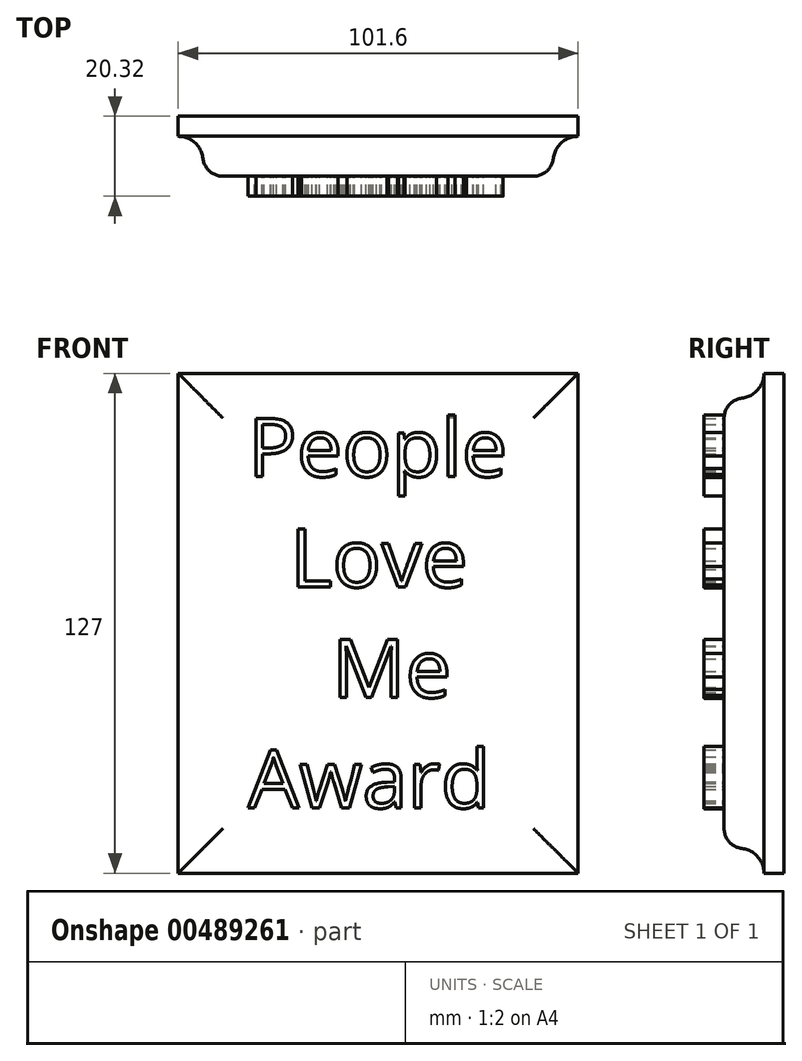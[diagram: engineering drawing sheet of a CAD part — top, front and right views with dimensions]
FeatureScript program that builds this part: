
annotation { "Feature Type Name" : "Feature", "Feature Type Description" : "" }
export const myFeature = defineFeature(function(context is Context, id is Id, definition is map)
    precondition{}
    {
        {
            var Q0;
            Q0=qCreatedBy(makeId("Front.planeOp"),FACE);
            var sketch = newSketch(context, id + "F0", { "sketchPlane" : qUnion([Q0])});
            skLineSegment(sketch, "E0.bottom", {"start": v(-101.6, 127) * mm, "end": v(0, 127) * mm});
            skLineSegment(sketch, "E0.top", {"start": v(-101.6, 0) * mm, "end": v(0, 0) * mm});
            skLineSegment(sketch, "E0.left", {"start": v(-101.6, 127) * mm, "end": v(-101.6, 0) * mm});
            skLineSegment(sketch, "E0.right", {"start": v(0, 127) * mm, "end": v(0, 0) * mm});
            skSolve(sketch);
        }
        {
            var Q0;
            Q0=qSketchRegion(id+"F0",true);
            extrude(context, id + "F1", {"entities" : qUnion([Q0]), "depth" : 15.24 * mm});
        }
        {
            var Q0;
            Q0=makeQuery(id+"F1.opExtrude","CAP_FACE",FACE,{"disambiguationData":[OSD([sQuery(id+"F0.wireOp",EDGE,"E0.bottom"),sQuery(id+"F0.wireOp",EDGE,"E0.top"),sQuery(id+"F0.wireOp",EDGE,"E0.left"),sQuery(id+"F0.wireOp",EDGE,"E0.right")])],"isStart":false});
            var sketch = newSketch(context, id + "F2", { "sketchPlane" : qUnion([Q0])});
            skLineSegment(sketch, "E1.bottom", {"start": v(-6.35, 6.35) * mm, "end": v(-95.25, 6.35) * mm});
            skLineSegment(sketch, "E1.top", {"start": v(-6.35, 120.65) * mm, "end": v(-95.25, 120.65) * mm});
            skLineSegment(sketch, "E1.left", {"start": v(-6.35, 6.35) * mm, "end": v(-6.35, 120.65) * mm});
            skLineSegment(sketch, "E1.right", {"start": v(-95.25, 6.35) * mm, "end": v(-95.25, 120.65) * mm});
            skLineSegment(sketch, "E2.bottom", {"start": v(-101.6, 127) * mm, "end": v(0, 127) * mm});
            skLineSegment(sketch, "E2.top", {"start": v(-101.6, 0) * mm, "end": v(0, 0) * mm});
            skLineSegment(sketch, "E2.left", {"start": v(-101.6, 127) * mm, "end": v(-101.6, 0) * mm});
            skLineSegment(sketch, "E2.right", {"start": v(0, 127) * mm, "end": v(0, 0) * mm});
            skSolve(sketch);
        }
        {
            var Q0;
            Q0=qSketchRegion(id+"F2",true);
            extrude(context, id + "F3", {"entities" : qUnion([Q0]), "operationType" : NewBodyOperationType.REMOVE, "oppositeDirection" : true, "depth" : 10.16 * mm});
        }
        {
            var Q0;
            Q0=makeQuery(id+"F3.boolean.opBoolean","COPY",EDGE,{"derivedFrom":makeQuery(id+"F3.opExtrude","CAP_EDGE",EDGE,{"disambiguationData":[OSD([sQuery(id+"F2.wireOp",EDGE,"E1.top")])],"isStart":false})});
            var Q1;
            Q1=makeQuery(id+"F3.boolean.opBoolean","COPY",EDGE,{"derivedFrom":makeQuery(id+"F3.opExtrude","CAP_EDGE",EDGE,{"disambiguationData":[OSD([sQuery(id+"F2.wireOp",EDGE,"E1.left")])],"isStart":false})});
            var Q2;
            Q2=makeQuery(id+"F3.boolean.opBoolean","COPY",EDGE,{"derivedFrom":makeQuery(id+"F3.opExtrude","CAP_EDGE",EDGE,{"disambiguationData":[OSD([sQuery(id+"F2.wireOp",EDGE,"E1.right")])],"isStart":false})});
            var Q3;
            Q3=makeQuery(id+"F3.boolean.opBoolean","COPY",EDGE,{"derivedFrom":makeQuery(id+"F3.opExtrude","CAP_EDGE",EDGE,{"disambiguationData":[OSD([sQuery(id+"F2.wireOp",EDGE,"E1.bottom")])],"isStart":false})});
            fillet(context, id + "F4", {"entities" : qUnion([Q0, Q1, Q2, Q3]), "radius" : 6.35 * mm, "tangentPropagation" : true, "allowEdgeOverflow" : false});
        }
        {
            var Q0;
            Q0=makeQuery(id+"F1.opExtrude","CAP_FACE",FACE,{"disambiguationData":[OSD([sQuery(id+"F0.wireOp",EDGE,"E0.bottom"),sQuery(id+"F0.wireOp",EDGE,"E0.top"),sQuery(id+"F0.wireOp",EDGE,"E0.left"),sQuery(id+"F0.wireOp",EDGE,"E0.right")])],"isStart":false});
            fillet(context, id + "F5", {"entities" : qUnion([Q0]), "radius" : 5.08 * mm, "tangentPropagation" : true, "allowEdgeOverflow" : false});
        }
        {
            var Q0;
            Q0=makeQuery(id+"F1.opExtrude","CAP_FACE",FACE,{"disambiguationData":[OSD([sQuery(id+"F0.wireOp",EDGE,"E0.bottom"),sQuery(id+"F0.wireOp",EDGE,"E0.top"),sQuery(id+"F0.wireOp",EDGE,"E0.left"),sQuery(id+"F0.wireOp",EDGE,"E0.right")])],"isStart":false});
            var sketch = newSketch(context, id + "F6", { "sketchPlane" : qUnion([Q0])});
            skText(sketch, "E3", { "text": "People\n  Love\n    Me\nAward", "fontName": "OpenSans-Regular.ttf"});
            const initialGuessF6  = {"E3": [-0.0839, 0.10078, 1, 0, 0.01486]};
            skSetInitialGuess(sketch, initialGuessF6);
            skSolve(sketch);
        }
        {
            var Q0;
            Q0=qSketchRegion(id+"F6",true);
            extrude(context, id + "F7", {"entities" : qUnion([Q0]), "operationType" : NewBodyOperationType.ADD, "depth" : 5.08 * mm});
        }
    });
